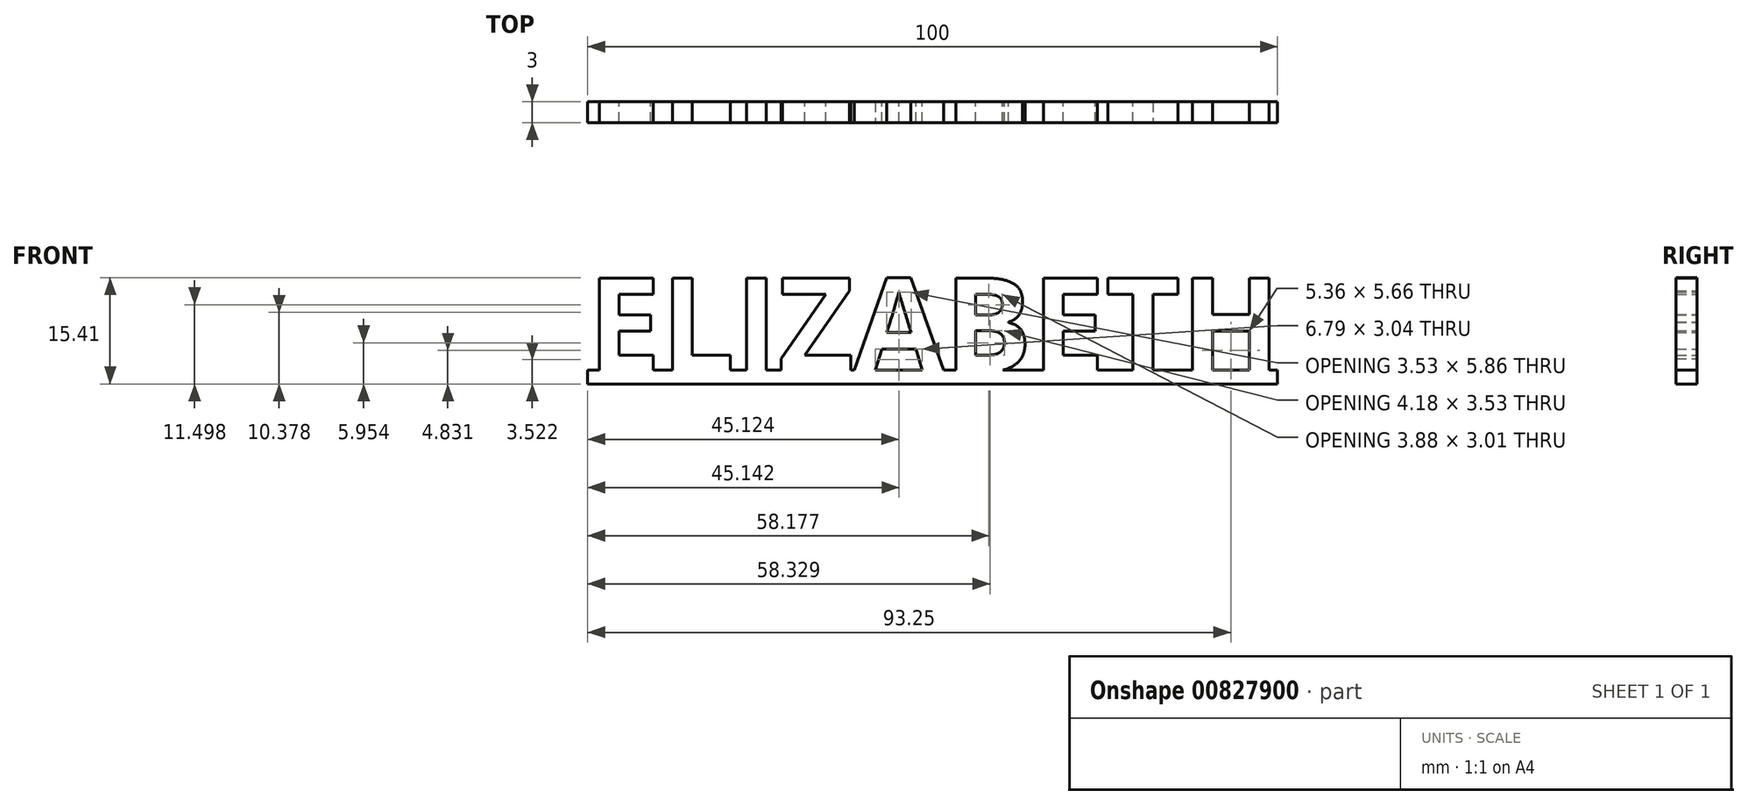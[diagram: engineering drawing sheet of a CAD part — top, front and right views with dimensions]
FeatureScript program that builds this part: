
annotation { "Feature Type Name" : "Feature", "Feature Type Description" : "" }
export const myFeature = defineFeature(function(context is Context, id is Id, definition is map)
    precondition{}
    {
        {
            var Q0;
            Q0=qCreatedBy(makeId("Front.planeOp"),FACE);
            var sketch = newSketch(context, id + "F0", { "sketchPlane" : qUnion([Q0])});
            skLineSegment(sketch, "E0.bottom", {"start": v(50, -1.82) * mm, "end": v(-50, -1.82) * mm});
            skLineSegment(sketch, "E0.top", {"start": v(50, 0.18) * mm, "end": v(-50, 0.18) * mm});
            skLineSegment(sketch, "E0.left", {"start": v(50, -1.82) * mm, "end": v(50, 0.18) * mm});
            skLineSegment(sketch, "E0.right", {"start": v(-50, -1.82) * mm, "end": v(-50, 0.18) * mm});
            skPoint(sketch, "E0.middle", {"position": v(0, -0.82) * mm});
            skSolve(sketch);
        }
        {
            var Q0;
            Q0=qCreatedBy(makeId("Front.planeOp"),FACE);
            var sketch = newSketch(context, id + "F1", { "sketchPlane" : qUnion([Q0])});
            skText(sketch, "E1", { "text": "ELIZABETH", "fontName": "OpenSans-Bold.ttf"});
            const initialGuessF1  = {"E1": [-0.05, 0, 1, 0, 0.01365]};
            skSetInitialGuess(sketch, initialGuessF1);
            skSolve(sketch);
        }
        {
            var Q0;
            Q0 = qSketchRegion(id + "F0", true);
            extrude(context, id + "F2", {"entities" : qUnion([Q0]), "depth" : 3 * mm, "offsetDistance" : 25.4 * mm});
        }
        {
            var Q0;
            Q0 = qSketchRegion(id + "F1", true);
            extrude(context, id + "F3", {"entities" : qUnion([Q0]), "operationType" : NewBodyOperationType.ADD, "depth" : 3 * mm, "offsetDistance" : 25.4 * mm});
        }
    });
